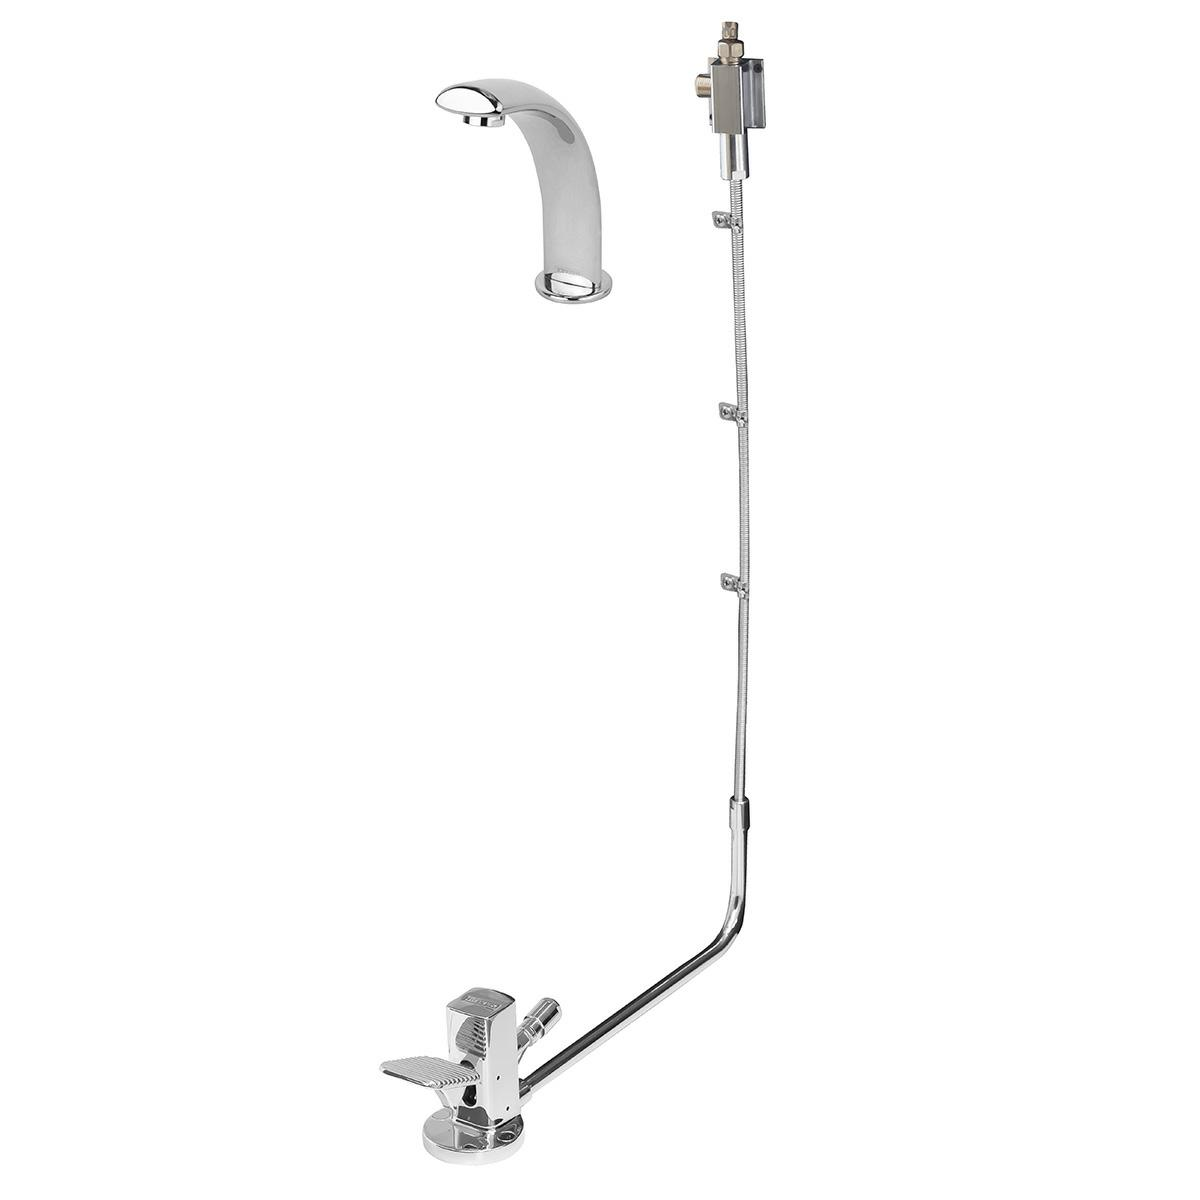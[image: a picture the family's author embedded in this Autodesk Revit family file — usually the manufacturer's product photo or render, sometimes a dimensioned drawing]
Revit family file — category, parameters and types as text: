
# Revit family: VP-1_RFA
name_source: partatom
category: Aparatos sanitarios
units: mm (PartAtom-declared; Revit-internal decimal feet)

## family parameters
Compartido = Sí
Corte con vacíos al cargar = No
Cota de conector redondo = Diámetro de uso
Número OmniClass = 23.45.55.14
Punto de cálculo de habitación = Sí
Se basa en plano de trabajo = Sí
Siempre vertical = Sí
Tipo de pieza = Normal
Título OmniClass = Single Faucets

## types (1)
- VP-1
    Accesorios = Conectores ½ -14 NPSM
    Características del Producto = Llave para lavabo con pedal expuesto, sin contra
    Comentarios de tipo = Monomando para lavabo.
    Cuerpo de Latón = Brass
    Descripción = Llave para lavabo con pedal expuesto
    Elevación por defecto = 1"
    Fabricante = HELVEX S.A. de C.V.
    Garantía = El producto HELVEX está garantizado como libre de defectos en materiales y procesos de fabricación. El producto HELVEX está garantizado, en lo que se refiere a los acabados; por un periodo de 10 años en los acabados cromo y duravex, y por 2 años en acabados diferentes al cromo, a partir de la fecha de compra indicada en la factura
    Hoja Técnica = https://www.helvex.com.mx
    Imagen de tipo = VP-1.jpg
    Instalación = Conexión ½ - 14 NPSM
    Instructivo = https://www.helvex.com.mx
    Modelo = VP-1
    Operación = Para abrir el flujo de agua oprima el pedal con el pie.
    Presión Máxima de Trabajo = 85.3 psi
    Presión Mínima de Trabajo = 3.6 psi
    Total Height = 7"
    Total Width = 2"
    URL = https://www.helvex.com.mx

## geometry (parser evidence)
native form markers: Sweep x3
no freeform markers — native parametric forms only
